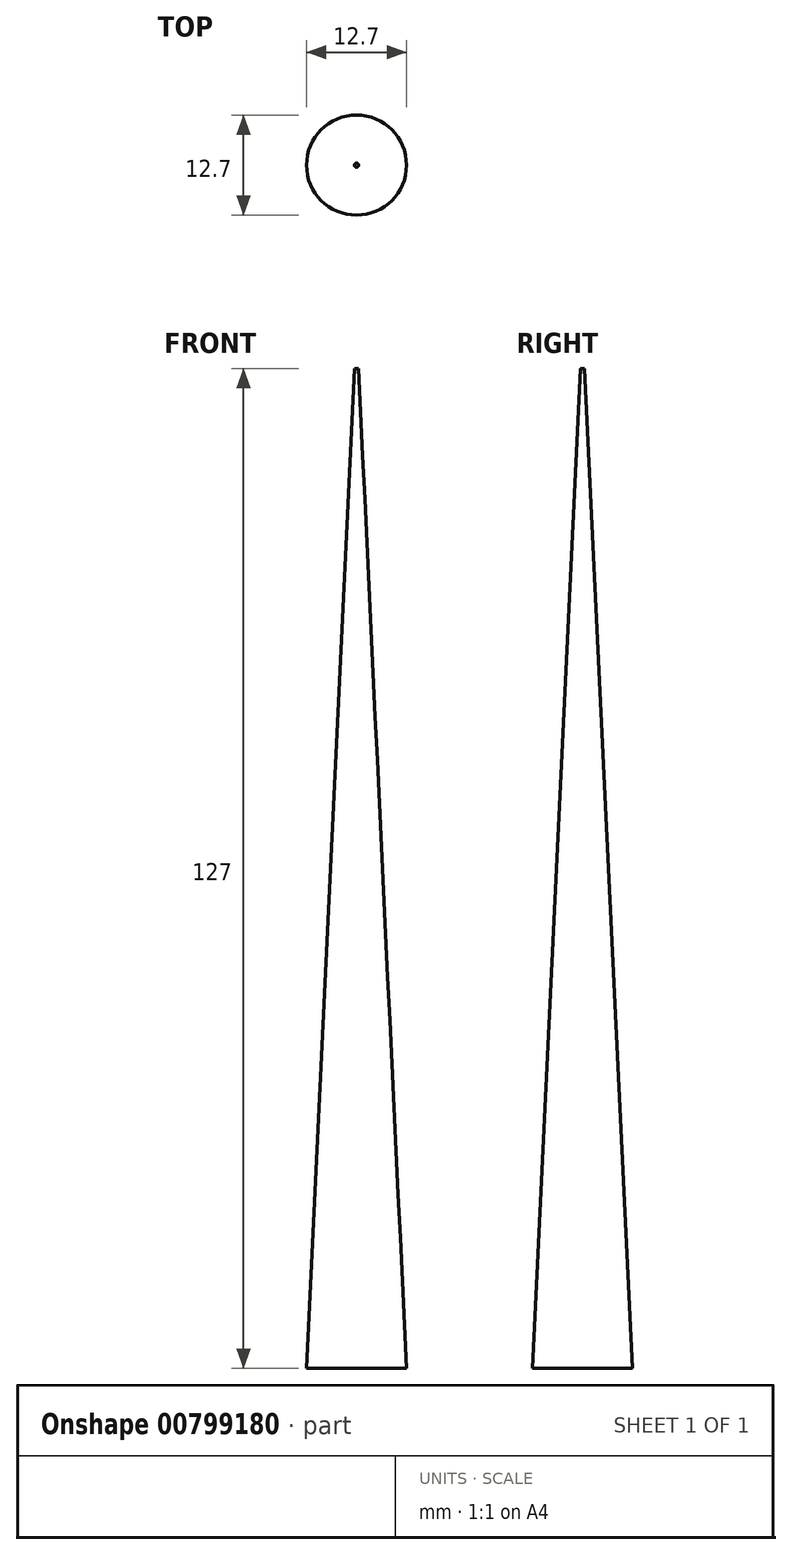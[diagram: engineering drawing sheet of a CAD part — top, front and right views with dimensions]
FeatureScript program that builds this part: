
annotation { "Feature Type Name" : "Feature", "Feature Type Description" : "" }
export const myFeature = defineFeature(function(context is Context, id is Id, definition is map)
    precondition{}
    {
        {
            var Q0;
            Q0=qCreatedBy(makeId("Top.planeOp"),FACE);
            var sketch = newSketch(context, id + "F0", { "sketchPlane" : qUnion([Q0])});
            skCircle(sketch, "E0", {"center": v(0, 0) * mm, "radius": 6.35 * mm});
            skSolve(sketch);
        }
        {
            var Q0;
            Q0=makeQuery(id+"F0.imprint","IMPRINT",FACE,{"disambiguationData":[TD([[makeQuery(id+"F0.imprint","IMPRINT",EDGE,{"derivedFrom":sQuery(id+"F0.wireOp",EDGE,"E0")}),1.0]])]});
            extrude(context, id + "F1", {"entities" : qUnion([Q0]), "depth" : 127 * mm, "offsetDistance" : 25.4 * mm});
        }
        {
            var Q0;
            Q0=qCreatedBy(makeId("Front.planeOp"),FACE);
            var sketch = newSketch(context, id + "F2", { "sketchPlane" : qUnion([Q0])});
            skLineSegment(sketch, "E1.bottom", {"start": v(0, 0) * mm, "end": v(6.35, 0) * mm});
            skLineSegment(sketch, "E1.top", {"start": v(0, 127) * mm, "end": v(6.35, 127) * mm});
            skLineSegment(sketch, "E1.left", {"start": v(0, 0) * mm, "end": v(0, 127) * mm});
            skLineSegment(sketch, "E1.right", {"start": v(6.35, 0) * mm, "end": v(6.35, 127) * mm});
            skPoint(sketch, "E2", {"position": v(0.25, 127) * mm});
            skLineSegment(sketch, "E3", {"start": v(0.25, 127) * mm, "end": v(6.35, 0) * mm});
            skSolve(sketch);
        }
        {
            var Q0;
            {var subQ0=sQuery(id+"F2.wireOp",EDGE,"E1.right");Q0=makeQuery(id+"F2.imprint","IMPRINT",FACE,{"disambiguationData":[TD([[makeQuery(id+"F2.imprint","IMPRINT",EDGE,{"derivedFrom":subQ0}),1.0]])]});}
            var Q1;
            Q1=sQuery(id+"F2.wireOp",EDGE,"E1.left");
            revolve(context, id + "F3", {"operationType" : NewBodyOperationType.REMOVE, "surfaceOperationType" : NewSurfaceOperationType.NEW, "entities" : qUnion([Q0]), "axis" : qUnion([Q1]), "revolveType" : RevolveType.FULL, "oppositeDirection" : true});
        }
    });
